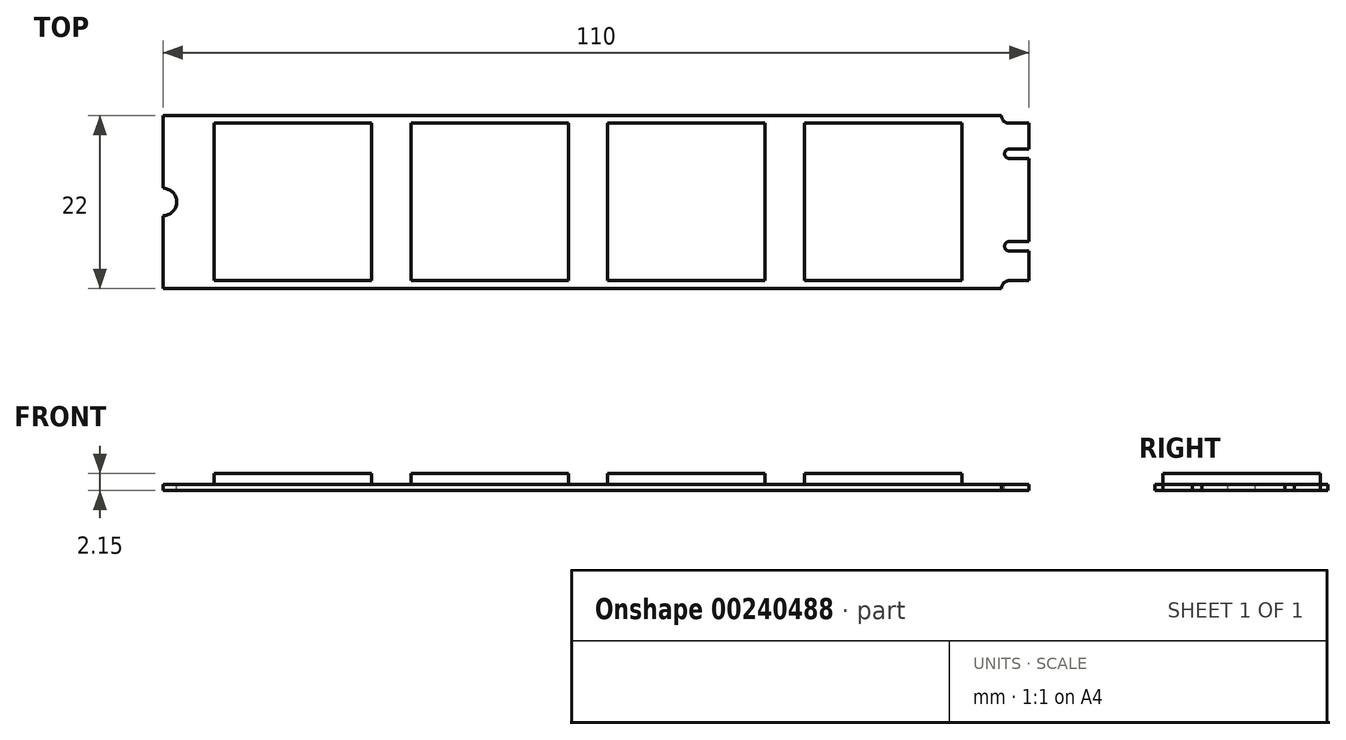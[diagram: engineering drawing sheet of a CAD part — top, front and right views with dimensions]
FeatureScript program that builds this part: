
annotation { "Feature Type Name" : "Feature", "Feature Type Description" : "" }
export const myFeature = defineFeature(function(context is Context, id is Id, definition is map)
    precondition{}
    {
        {
            var Q0;
            Q0=qCreatedBy(makeId("Top.planeOp"),FACE);
            var sketch = newSketch(context, id + "F0", { "sketchPlane" : qUnion([Q0])});
            skLineSegment(sketch, "E0.bottom", {"start": v(55, -11) * mm, "end": v(-55, -11) * mm});
            skLineSegment(sketch, "E0.top", {"start": v(55, 11) * mm, "end": v(-55, 11) * mm});
            skLineSegment(sketch, "E0.left", {"start": v(55, -11) * mm, "end": v(55, 11) * mm});
            skLineSegment(sketch, "E0.right", {"start": v(-55, -11) * mm, "end": v(-55, 11) * mm});
            skPoint(sketch, "E0.middle", {"position": v(0, 0) * mm});
            skSolve(sketch);
        }
        {
            var Q0;
            Q0 = qSketchRegion(id + "F0", true);
            extrude(context, id + "F1", {"entities" : qUnion([Q0]), "depth" : .8 * mm});
        }
        {
            var Q0;
            Q0=makeQuery(id+"F1.opExtrude","CAP_FACE",FACE,{"disambiguationData":[OSD([sQuery(id+"F0.wireOp",EDGE,"E0.bottom"),sQuery(id+"F0.wireOp",EDGE,"E0.top"),sQuery(id+"F0.wireOp",EDGE,"E0.left"),sQuery(id+"F0.wireOp",EDGE,"E0.right")])],"isStart":false});
            var sketch = newSketch(context, id + "F2", { "sketchPlane" : qUnion([Q0])});
            skArc(sketch, "E1", {"start": v(-55, -1.75) * mm, "mid": v(-53.25, 0) * mm, "end": v(-55, 1.75) * mm});
            skLineSegment(sketch, "E2.bottom", {"start": v(55, 11) * mm, "end": v(51.5, 11) * mm});
            skLineSegment(sketch, "E2.top", {"start": v(55, 10) * mm, "end": v(51.5, 10) * mm});
            skLineSegment(sketch, "E2.left", {"start": v(55, 11) * mm, "end": v(55, 10) * mm});
            skLineSegment(sketch, "E2.right", {"start": v(51.5, 11) * mm, "end": v(51.5, 10) * mm});
            skLineSegment(sketch, "E3", {"start": v(55, 0) * mm, "end": v(51.5, 0) * mm, "construction": true});
            skLineSegment(sketch, "E4.MirrorCS", {"start": v(55, -10) * mm, "end": v(51.5, -10) * mm});
            skLineSegment(sketch, "E5.MirrorCS", {"start": v(51.5, -11) * mm, "end": v(51.5, -10) * mm});
            skLineSegment(sketch, "E6.MirrorCS", {"start": v(55, -11) * mm, "end": v(51.5, -11) * mm});
            skLineSegment(sketch, "E7.MirrorCS", {"start": v(55, -11) * mm, "end": v(55, -10) * mm});
            skLineSegment(sketch, "E8", {"start": v(55, 0) * mm, "end": v(55, 6.12) * mm, "construction": true});
            skLineSegment(sketch, "E9", {"start": v(55, 0) * mm, "end": v(55, -5.62) * mm, "construction": true});
            skLineSegment(sketch, "E10", {"start": v(55, 6.12) * mm, "end": v(52.5, 6.12) * mm, "construction": true});
            skLineSegment(sketch, "E11", {"start": v(55, -5.62) * mm, "end": v(52.5, -5.62) * mm, "construction": true});
            skArc(sketch, "E12", {"start": v(52.5, -5.03) * mm, "mid": v(51.9, -5.62) * mm, "end": v(52.5, -6.22) * mm});
            skArc(sketch, "E13", {"start": v(52.5, 6.72) * mm, "mid": v(51.9, 6.12) * mm, "end": v(52.5, 5.53) * mm});
            skLineSegment(sketch, "E14.bottom", {"start": v(52.5, -5.03) * mm, "end": v(55, -5.03) * mm});
            skLineSegment(sketch, "E14.top", {"start": v(52.5, -6.22) * mm, "end": v(55, -6.22) * mm});
            skLineSegment(sketch, "E14.left", {"start": v(52.5, -5.03) * mm, "end": v(52.5, -6.22) * mm});
            skLineSegment(sketch, "E14.right", {"start": v(55, -5.03) * mm, "end": v(55, -6.22) * mm});
            skLineSegment(sketch, "E15.bottom", {"start": v(52.5, 6.72) * mm, "end": v(55, 6.72) * mm});
            skLineSegment(sketch, "E15.top", {"start": v(52.5, 5.53) * mm, "end": v(55, 5.53) * mm});
            skLineSegment(sketch, "E15.left", {"start": v(52.5, 6.72) * mm, "end": v(52.5, 5.53) * mm});
            skLineSegment(sketch, "E15.right", {"start": v(55, 6.72) * mm, "end": v(55, 5.53) * mm});
            skLineSegment(sketch, "E16", {"start": v(-55, 1.75) * mm, "end": v(-55, -1.75) * mm});
            skLineSegment(sketch, "E17", {"start": v(51.5, 0) * mm, "end": v(46.5, 0) * mm, "construction": true});
            skLineSegment(sketch, "E18.bottom", {"start": v(46.5, 10) * mm, "end": v(26.5, 10) * mm});
            skLineSegment(sketch, "E18.top", {"start": v(46.5, -10) * mm, "end": v(26.5, -10) * mm});
            skLineSegment(sketch, "E18.left", {"start": v(46.5, 10) * mm, "end": v(46.5, -10) * mm});
            skLineSegment(sketch, "E18.right", {"start": v(26.5, 10) * mm, "end": v(26.5, -10) * mm});
            skLineSegment(sketch, "E19.1.0.0", {"start": v(1.5, 10) * mm, "end": v(1.5, -10) * mm});
            skLineSegment(sketch, "E19.1.0.1", {"start": v(21.5, 10) * mm, "end": v(1.5, 10) * mm});
            skLineSegment(sketch, "E19.1.0.2", {"start": v(21.5, -10) * mm, "end": v(1.5, -10) * mm});
            skLineSegment(sketch, "E19.1.0.3", {"start": v(21.5, 10) * mm, "end": v(21.5, -10) * mm});
            skLineSegment(sketch, "E19.2.0.0", {"start": v(-23.5, 10) * mm, "end": v(-23.5, -10) * mm});
            skLineSegment(sketch, "E19.2.0.1", {"start": v(-3.5, 10) * mm, "end": v(-23.5, 10) * mm});
            skLineSegment(sketch, "E19.2.0.2", {"start": v(-3.5, -10) * mm, "end": v(-23.5, -10) * mm});
            skLineSegment(sketch, "E19.2.0.3", {"start": v(-3.5, 10) * mm, "end": v(-3.5, -10) * mm});
            skLineSegment(sketch, "E19.3.0.0", {"start": v(-48.5, 10) * mm, "end": v(-48.5, -10) * mm});
            skLineSegment(sketch, "E19.3.0.1", {"start": v(-28.5, 10) * mm, "end": v(-48.5, 10) * mm});
            skLineSegment(sketch, "E19.3.0.2", {"start": v(-28.5, -10) * mm, "end": v(-48.5, -10) * mm});
            skLineSegment(sketch, "E19.3.0.3", {"start": v(-28.5, 10) * mm, "end": v(-28.5, -10) * mm});
            skLineSegment(sketch, "E19.direction1", {"start": v(26.5, -10) * mm, "end": v(1.5, -10) * mm, "construction": true});
            skSolve(sketch);
        }
        {
            var Q0;
            Q0=makeQuery(id+"F2.imprint","IMPRINT",FACE,{"disambiguationData":[TD([[makeQuery(id+"F2.imprint","IMPRINT",EDGE,{"derivedFrom":sQuery(id+"F2.wireOp",EDGE,"E1")}),1.0]])]});
            var Q1;
            Q1=makeQuery(id+"F2.imprint","IMPRINT",FACE,{"disambiguationData":[TD([[makeQuery(id+"F2.imprint","IMPRINT",EDGE,{"derivedFrom":sQuery(id+"F2.wireOp",EDGE,"E2.bottom")}),1.0]])]});
            var Q2;
            Q2=makeQuery(id+"F2.imprint","IMPRINT",FACE,{"disambiguationData":[TD([[makeQuery(id+"F2.imprint","IMPRINT",EDGE,{"derivedFrom":sQuery(id+"F2.wireOp",EDGE,"E4.MirrorCS")}),1.0]])]});
            var Q3;
            Q3=makeQuery(id+"F2.imprint","IMPRINT",FACE,{"disambiguationData":[TD([[makeQuery(id+"F2.imprint","IMPRINT",EDGE,{"derivedFrom":sQuery(id+"F2.wireOp",EDGE,"E12")}),1.0]])]});
            var Q4;
            Q4=makeQuery(id+"F2.imprint","IMPRINT",FACE,{"disambiguationData":[TD([[makeQuery(id+"F2.imprint","IMPRINT",EDGE,{"derivedFrom":sQuery(id+"F2.wireOp",EDGE,"E13")}),1.0]])]});
            var Q5;
            Q5=makeQuery(id+"F2.imprint","IMPRINT",FACE,{"disambiguationData":[TD([[makeQuery(id+"F2.imprint","IMPRINT",EDGE,{"derivedFrom":sQuery(id+"F2.wireOp",EDGE,"E14.bottom")}),-1.0]])]});
            var Q6;
            Q6=makeQuery(id+"F2.imprint","IMPRINT",FACE,{"disambiguationData":[TD([[makeQuery(id+"F2.imprint","IMPRINT",EDGE,{"derivedFrom":sQuery(id+"F2.wireOp",EDGE,"E15.bottom")}),-1.0]])]});
            extrude(context, id + "F3", {"entities" : qUnion([Q0, Q1, Q2, Q3, Q4, Q5, Q6]), "operationType" : NewBodyOperationType.REMOVE, "endBound" : BoundingType.THROUGH_ALL, "oppositeDirection" : true, "depth" : 25 * mm});
        }
        {
            var Q0;
            Q0=makeQuery(id+"F3.boolean.opBoolean","COPY",EDGE,{"derivedFrom":makeQuery(id+"F3.opExtrude","SWEPT_EDGE",EDGE,{"disambiguationData":[OSD([sQuery(id+"F2.wireOp",EDGE,"E4.MirrorCS"),sQuery(id+"F2.wireOp",EDGE,"E5.MirrorCS")])]})});
            var Q1;
            Q1=makeQuery(id+"F3.boolean.opBoolean","COPY",EDGE,{"derivedFrom":makeQuery(id+"F3.opExtrude","SWEPT_EDGE",EDGE,{"disambiguationData":[OSD([sQuery(id+"F2.wireOp",EDGE,"E2.top"),sQuery(id+"F2.wireOp",EDGE,"E2.right")])]})});
            fillet(context, id + "F4", {"entities" : qUnion([Q0, Q1]), "radius" : 1 * mm, "tangentPropagation" : true, "allowEdgeOverflow" : false});
        }
        {
            var Q0;
            Q0=makeQuery(id+"F2.imprint","IMPRINT",FACE,{"disambiguationData":[TD([[makeQuery(id+"F2.imprint","IMPRINT",EDGE,{"derivedFrom":sQuery(id+"F2.wireOp",EDGE,"E18.bottom")}),1.0]])]});
            var Q1;
            Q1=makeQuery(id+"F2.imprint","IMPRINT",FACE,{"disambiguationData":[TD([[makeQuery(id+"F2.imprint","IMPRINT",EDGE,{"derivedFrom":sQuery(id+"F2.wireOp",EDGE,"E19.1.0.0")}),1.0]])]});
            var Q2;
            Q2=makeQuery(id+"F2.imprint","IMPRINT",FACE,{"disambiguationData":[TD([[makeQuery(id+"F2.imprint","IMPRINT",EDGE,{"derivedFrom":sQuery(id+"F2.wireOp",EDGE,"E19.2.0.0")}),1.0]])]});
            var Q3;
            Q3=makeQuery(id+"F2.imprint","IMPRINT",FACE,{"disambiguationData":[TD([[makeQuery(id+"F2.imprint","IMPRINT",EDGE,{"derivedFrom":sQuery(id+"F2.wireOp",EDGE,"E19.3.0.0")}),1.0]])]});
            extrude(context, id + "F5", {"entities" : qUnion([Q0, Q1, Q2, Q3]), "operationType" : NewBodyOperationType.ADD, "depth" : 1.35 * mm});
        }
    });
